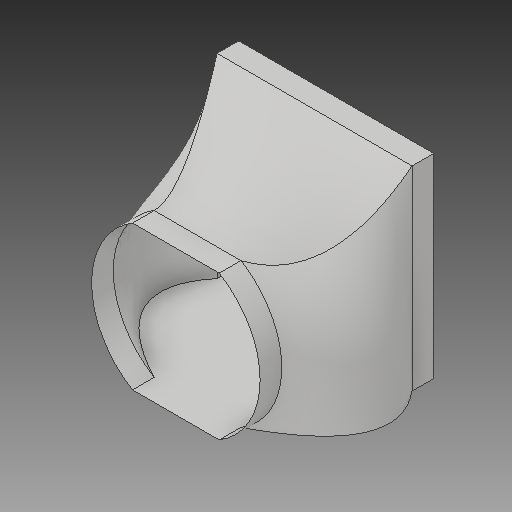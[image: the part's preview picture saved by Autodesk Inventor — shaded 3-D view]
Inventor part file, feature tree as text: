
AUTODESK INVENTOR PART (.ipt)
format: ipt  version: 2017 (Build 210142000, 142)  size: 334,848 bytes
history: native  units: in
note: dims shown in document units (in); Inventor stores cm internally (conversion verified against a paired STEP export)
features: extrude x2, other x2, sketch x2, loft x2, delete_face x1
ambient origin geometry x8: Origin, YZ Plane, XZ Plane, XY Plane, X Axis, Y Axis, Z Axis, Center Point
bodies: Solid1 (feature_tree)
feature tree (9):
  extrude  "connection"  Depth=2.7in
  other  "front half of room"
  other  "front of room"
  sketch  "Sketch3"  dims[d12=1.0in d13=0.0in d14=2.7in]
  loft  "shell make "
  loft  "shell cut"
  extrude  "connection to door"  Depth=9.0in
  delete_face  "Delete Face3"
  sketch  "Sketch5"  dims[d17=2.7in d26=69.0in d27=59.0in d33=1.0in d34=1.0in d35=1.0in d36=1.0in d153=6.21in d154=5.31in d157=0.0in d158=90.0deg d159=0.0in d160=90.0deg d161=0.0in d162=90.0deg d180=0.0in d181=90.0deg d182=0.0in d183=90.0deg d184=0.0in d185=90.0deg d217=3.082in d219=1.0in d220=1.0in d221=9.0in d222=9.0in d223=1.0in d241=1.0in d242=1.0in d243=1.0in d244=1.0in d245=1.0in d246=0.0in d262=4.0in d263=1.0in d264=4.8944in d266=3.8873in d267=3.8873in d271=1.6458in]
